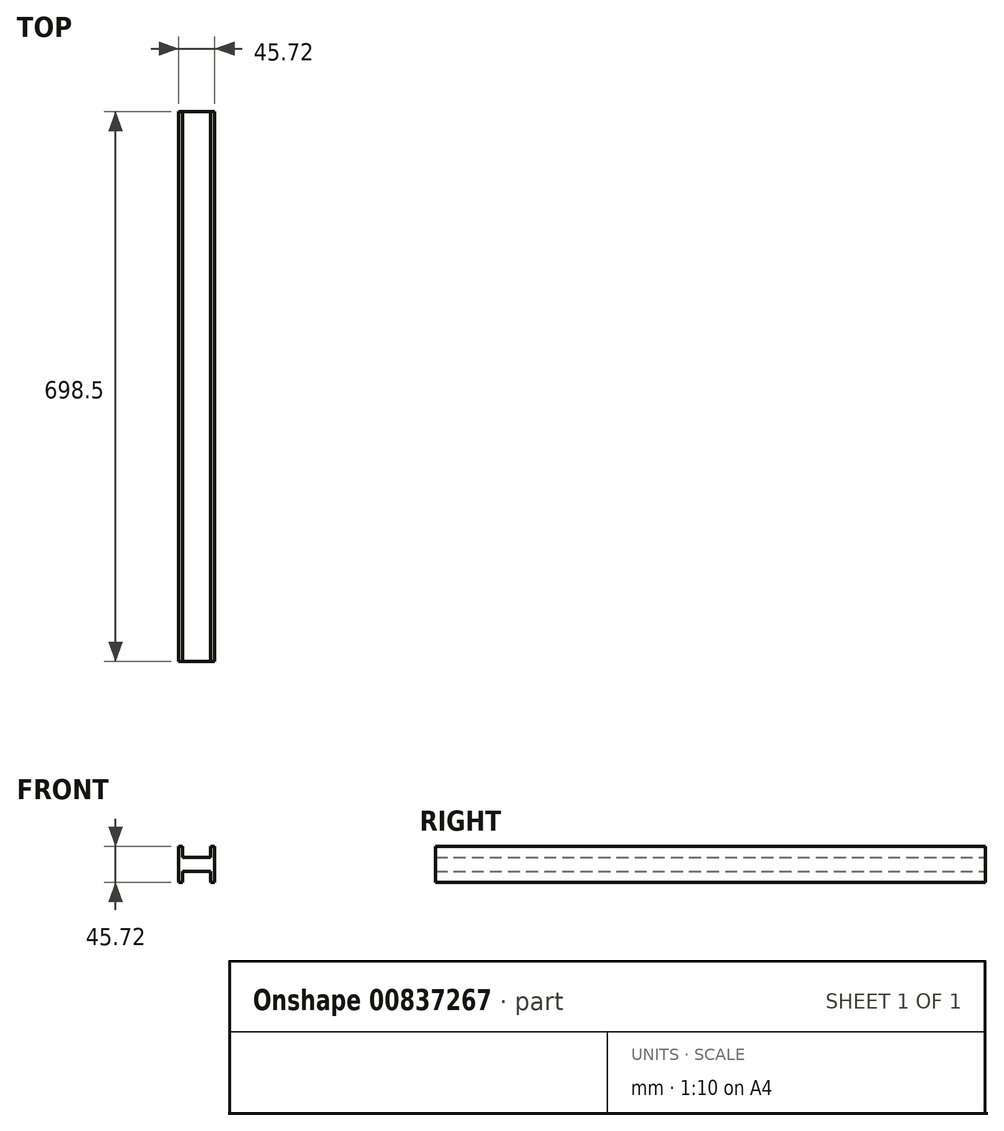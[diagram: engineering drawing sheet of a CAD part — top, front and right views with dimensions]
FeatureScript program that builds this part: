
annotation { "Feature Type Name" : "Feature", "Feature Type Description" : "" }
export const myFeature = defineFeature(function(context is Context, id is Id, definition is map)
    precondition{}
    {
        {
            var Q0;
            Q0=qCreatedBy(makeId("Front.planeOp"),FACE);
            var sketch = newSketch(context, id + "F0", { "sketchPlane" : qUnion([Q0])});
            skLineSegment(sketch, "E0.bottom", {"start": v(22.86, 22.86) * mm, "end": v(17.8, 22.86) * mm});
            skLineSegment(sketch, "E0.top", {"start": v(22.86, -22.86) * mm, "end": v(17.8, -22.86) * mm});
            skLineSegment(sketch, "E0.left", {"start": v(22.86, 22.86) * mm, "end": v(22.86, -22.86) * mm});
            skLineSegment(sketch, "E0.right", {"start": v(-22.86, 22.86) * mm, "end": v(-22.86, -22.86) * mm});
            skPoint(sketch, "E0.middle", {"position": v(0, 0) * mm});
            skLineSegment(sketch, "E1.top", {"start": v(-18.22, 8.64) * mm, "end": v(17.8, 8.64) * mm});
            skLineSegment(sketch, "E1.left", {"start": v(-18.22, 22.86) * mm, "end": v(-18.22, 8.64) * mm});
            skLineSegment(sketch, "E1.right", {"start": v(17.8, 22.86) * mm, "end": v(17.8, 8.64) * mm});
            skLineSegment(sketch, "E2", {"start": v(-65.42, 0) * mm, "end": v(65.2, 0) * mm, "construction": true});
            skLineSegment(sketch, "E3.MirrorCS", {"start": v(-18.22, -22.86) * mm, "end": v(-18.22, -8.64) * mm});
            skLineSegment(sketch, "E4.MirrorCS", {"start": v(-18.22, -8.64) * mm, "end": v(17.8, -8.64) * mm});
            skLineSegment(sketch, "E5.MirrorCS", {"start": v(17.8, -22.86) * mm, "end": v(17.8, -8.64) * mm});
            skLineSegment(sketch, "E6.trimOffspring", {"start": v(-18.22, 22.86) * mm, "end": v(-22.86, 22.86) * mm});
            skPoint(sketch, "E7.orphan", {"position": v(17.8, -31.29) * mm});
            skLineSegment(sketch, "E8.trimOffspring", {"start": v(-18.22, -22.86) * mm, "end": v(-22.86, -22.86) * mm});
            skPoint(sketch, "E9.orphan", {"position": v(-18.22, -31.29) * mm});
            skSolve(sketch);
        }
        {
            var Q0;
            Q0=qSketchRegion(id+"F0",true);
            extrude(context, id + "F1", {"entities" : qUnion([Q0]), "endBound" : BoundingType.SYMMETRIC, "depth" : 698.5 * mm, "offsetDistance" : 25.4 * mm});
        }
    });
